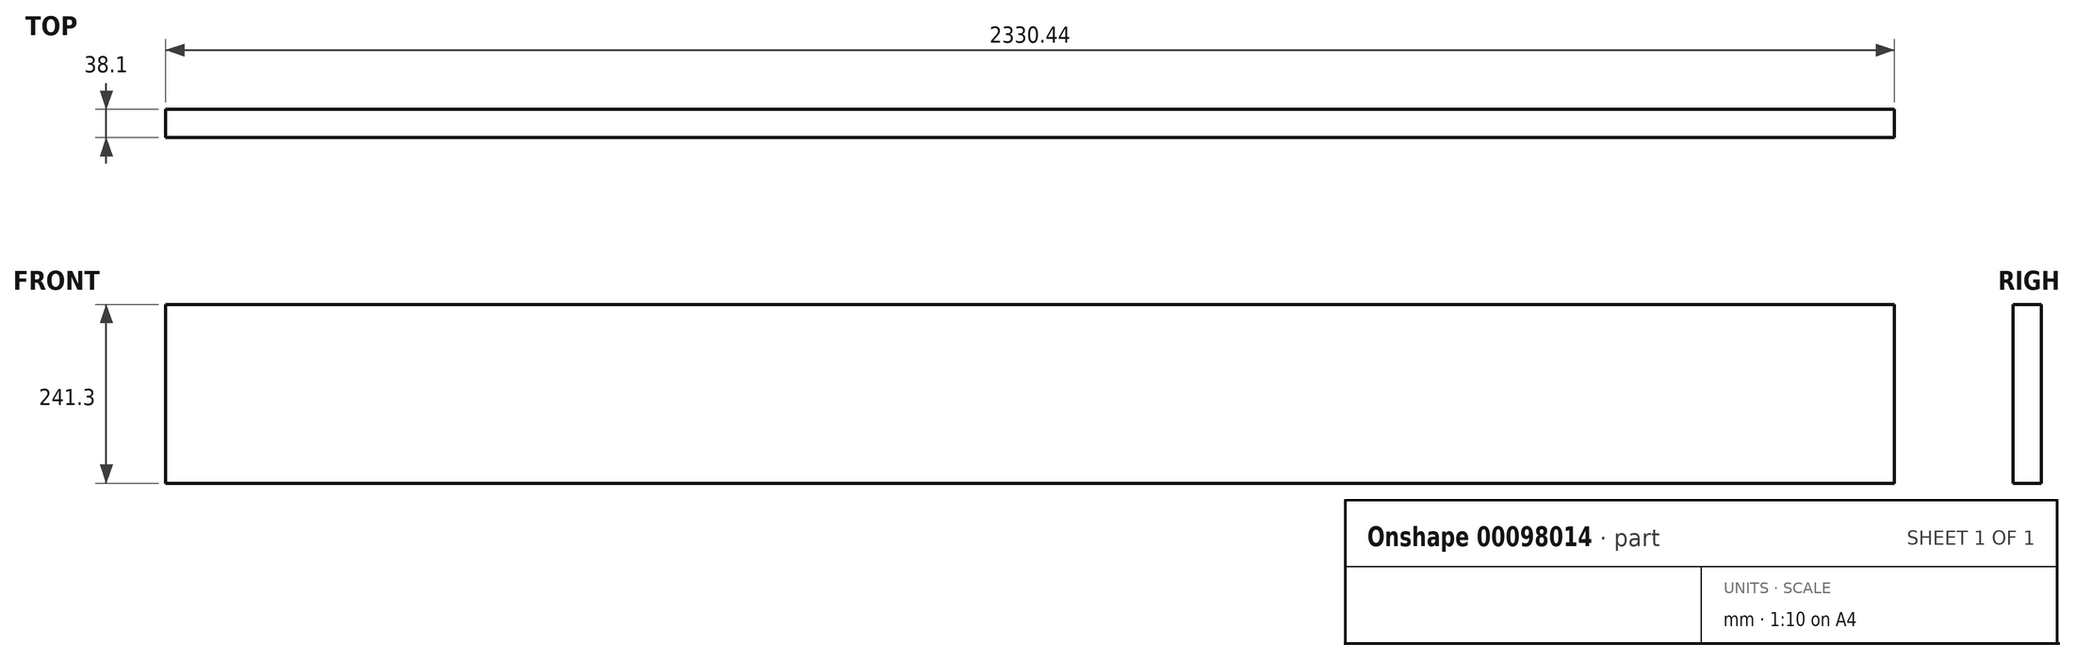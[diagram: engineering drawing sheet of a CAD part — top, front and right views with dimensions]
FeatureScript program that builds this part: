
annotation { "Feature Type Name" : "Feature", "Feature Type Description" : "" }
export const myFeature = defineFeature(function(context is Context, id is Id, definition is map)
    precondition{}
    {
        {
            var Q0;
            Q0=qCreatedBy(makeId("Front.planeOp"),FACE);
            var sketch = newSketch(context, id + "F0", { "sketchPlane" : qUnion([Q0])});
            skLineSegment(sketch, "E0.bottom", {"start": v(1165.23, 120.65) * mm, "end": v(-1165.23, 120.65) * mm});
            skLineSegment(sketch, "E0.top", {"start": v(1165.23, -120.65) * mm, "end": v(-1165.23, -120.65) * mm});
            skLineSegment(sketch, "E0.left", {"start": v(1165.23, 120.65) * mm, "end": v(1165.23, -120.65) * mm});
            skLineSegment(sketch, "E0.right", {"start": v(-1165.23, 120.65) * mm, "end": v(-1165.23, -120.65) * mm});
            skPoint(sketch, "E0.middle", {"position": v(0, 0) * mm});
            skSolve(sketch);
        }
        {
            var Q0;
            Q0=makeQuery(id+"F0.imprint","IMPRINT",FACE,{"disambiguationData":[TD([[makeQuery(id+"F0.imprint","IMPRINT",EDGE,{"derivedFrom":sQuery(id+"F0.wireOp",EDGE,"E0.bottom")}),1.0]])]});
            extrude(context, id + "F1", {"entities" : qUnion([Q0]), "depth" : 38.1 * mm});
        }
    });
